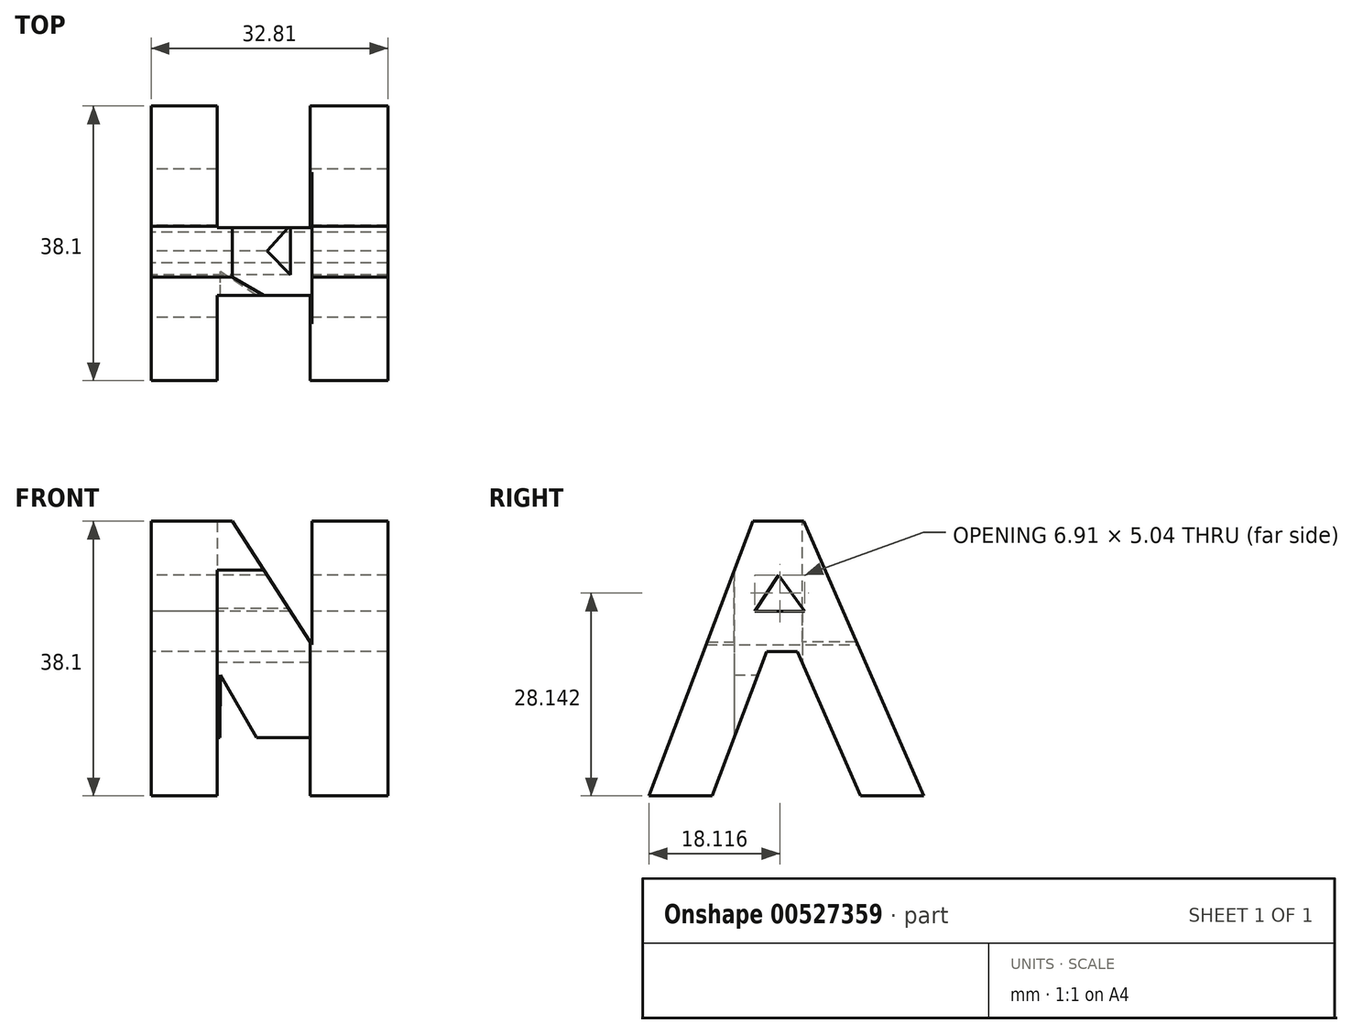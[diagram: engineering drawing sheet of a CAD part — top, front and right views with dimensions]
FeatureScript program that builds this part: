
annotation { "Feature Type Name" : "Feature", "Feature Type Description" : "" }
export const myFeature = defineFeature(function(context is Context, id is Id, definition is map)
    precondition{}
    {
        {
            var Q0;
            Q0=qCreatedBy(makeId("Front.planeOp"),FACE);
            var sketch = newSketch(context, id + "F0", { "sketchPlane" : qUnion([Q0])});
            skLineSegment(sketch, "E0", {"start": v(0, 0) * mm, "end": v(38.1, 0) * mm});
            skLineSegment(sketch, "E1", {"start": v(38.1, 0) * mm, "end": v(38.1, 38.1) * mm});
            skLineSegment(sketch, "E2", {"start": v(38.1, 38.1) * mm, "end": v(0, 38.1) * mm});
            skLineSegment(sketch, "E3", {"start": v(0, 38.1) * mm, "end": v(0, 0) * mm});
            skSolve(sketch);
        }
        {
            var Q0;
            Q0=qSketchRegion(id+"F0",true);
            extrude(context, id + "F1", {"entities" : qUnion([Q0]), "depth" : 38.1 * mm});
        }
        {
            var Q0;
            Q0=qCreatedBy(makeId("Right.planeOp"),FACE);
            var sketch = newSketch(context, id + "F2", { "sketchPlane" : qUnion([Q0])});
            skLineSegment(sketch, "E4", {"start": v(0, 0) * mm, "end": v(0, 38.1) * mm});
            skLineSegment(sketch, "E5", {"start": v(0, 38.1) * mm, "end": v(-38.1, 38.1) * mm});
            skLineSegment(sketch, "E6", {"start": v(-38.1, 38.1) * mm, "end": v(-38.1, 0) * mm});
            skLineSegment(sketch, "E7", {"start": v(-38.1, 0) * mm, "end": v(0, 0) * mm});
            skLineSegment(sketch, "E8", {"start": v(-38.1, 0) * mm, "end": v(-23.73, 38.1) * mm});
            skLineSegment(sketch, "E9", {"start": v(0, 0) * mm, "end": v(-16.67, 38.1) * mm});
            skLineSegment(sketch, "E10", {"start": v(-29.34, 0) * mm, "end": v(-21.78, 20.02) * mm});
            skLineSegment(sketch, "E11", {"start": v(-21.78, 20.02) * mm, "end": v(-17.52, 20.02) * mm});
            skLineSegment(sketch, "E12", {"start": v(-17.52, 20.02) * mm, "end": v(-8.76, 0) * mm});
            skLineSegment(sketch, "E13", {"start": v(-20.13, 25.62) * mm, "end": v(-16.53, 25.62) * mm});
            skLineSegment(sketch, "E14", {"start": v(-16.53, 25.62) * mm, "end": v(-20.13, 30.66) * mm});
            skLineSegment(sketch, "E15", {"start": v(-20.13, 30.66) * mm, "end": v(-23.44, 25.62) * mm});
            skLineSegment(sketch, "E16", {"start": v(-23.44, 25.62) * mm, "end": v(-20.13, 25.62) * mm});
            skSolve(sketch);
        }
        {
            var Q0;
            {var subQ0=sQuery(id+"F2.wireOp",EDGE,"E6");Q0=makeQuery(id+"F2.imprint","IMPRINT",FACE,{"disambiguationData":[TD([[makeQuery(id+"F2.imprint","IMPRINT",EDGE,{"derivedFrom":subQ0}),1.0]])]});}
            var Q1;
            {var subQ0=sQuery(id+"F2.wireOp",EDGE,"E10");Q1=makeQuery(id+"F2.imprint","IMPRINT",FACE,{"disambiguationData":[TD([[makeQuery(id+"F2.imprint","IMPRINT",EDGE,{"derivedFrom":subQ0}),-1.0]])]});}
            var Q2;
            {var subQ0=sQuery(id+"F2.wireOp",EDGE,"E4");Q2=makeQuery(id+"F2.imprint","IMPRINT",FACE,{"disambiguationData":[TD([[makeQuery(id+"F2.imprint","IMPRINT",EDGE,{"derivedFrom":subQ0}),1.0]])]});}
            var Q3;
            Q3=makeQuery(id+"F2.imprint","IMPRINT",FACE,{"disambiguationData":[TD([[makeQuery(id+"F2.imprint","IMPRINT",EDGE,{"derivedFrom":sQuery(id+"F2.wireOp",EDGE,"E13")}),1.0]])]});
            extrude(context, id + "F3", {"entities" : qUnion([Q0, Q1, Q2, Q3]), "operationType" : NewBodyOperationType.REMOVE, "depth" : 38.1 * mm});
        }
        {
            var Q0;
            Q0=qCreatedBy(makeId("Front.planeOp"),FACE);
            var sketch = newSketch(context, id + "F4", { "sketchPlane" : qUnion([Q0])});
            skLineSegment(sketch, "E17", {"start": v(0, 0) * mm, "end": v(38.1, 0) * mm});
            skLineSegment(sketch, "E18", {"start": v(38.1, 0) * mm, "end": v(38.1, 38.1) * mm});
            skLineSegment(sketch, "E19", {"start": v(38.1, 38.1) * mm, "end": v(0, 38.1) * mm});
            skLineSegment(sketch, "E20", {"start": v(0, 38.1) * mm, "end": v(0, 0) * mm});
            skLineSegment(sketch, "E21", {"start": v(13.19, 38.1) * mm, "end": v(24.25, 20.99) * mm});
            skLineSegment(sketch, "E22", {"start": v(11.37, 0) * mm, "end": v(11.56, 16.82) * mm});
            skLineSegment(sketch, "E23", {"start": v(11.56, 16.82) * mm, "end": v(21.16, 0) * mm});
            skLineSegment(sketch, "E24", {"start": v(24.25, 20.99) * mm, "end": v(24.25, 38.1) * mm});
            skLineSegment(sketch, "E25", {"start": v(34.76, 38.1) * mm, "end": v(34.76, 0) * mm});
            skLineSegment(sketch, "E26", {"start": v(1.95, 38.1) * mm, "end": v(1.95, 0) * mm});
            skSolve(sketch);
        }
        {
            var Q0;
            {var subQ0=sQuery(id+"F4.wireOp",EDGE,"E18");Q0=makeQuery(id+"F4.imprint","IMPRINT",FACE,{"disambiguationData":[TD([[makeQuery(id+"F4.imprint","IMPRINT",EDGE,{"derivedFrom":subQ0}),1.0]])]});}
            var Q1;
            {var subQ0=sQuery(id+"F4.wireOp",EDGE,"E21");Q1=makeQuery(id+"F4.imprint","IMPRINT",FACE,{"disambiguationData":[TD([[makeQuery(id+"F4.imprint","IMPRINT",EDGE,{"derivedFrom":subQ0}),1.0]])]});}
            var Q2;
            {var subQ0=sQuery(id+"F4.wireOp",EDGE,"E22");Q2=makeQuery(id+"F4.imprint","IMPRINT",FACE,{"disambiguationData":[TD([[makeQuery(id+"F4.imprint","IMPRINT",EDGE,{"derivedFrom":subQ0}),-1.0]])]});}
            var Q3;
            {var subQ0=sQuery(id+"F4.wireOp",EDGE,"E20");Q3=makeQuery(id+"F4.imprint","IMPRINT",FACE,{"disambiguationData":[TD([[makeQuery(id+"F4.imprint","IMPRINT",EDGE,{"derivedFrom":subQ0}),1.0]])]});}
            extrude(context, id + "F5", {"entities" : qUnion([Q0, Q1, Q2, Q3]), "operationType" : NewBodyOperationType.REMOVE, "depth" : 38.1 * mm});
        }
        {
            var Q0;
            Q0=qCreatedBy(makeId("Top.planeOp"),FACE);
            var sketch = newSketch(context, id + "F6", { "sketchPlane" : qUnion([Q0])});
            skLineSegment(sketch, "E27", {"start": v(0, 0) * mm, "end": v(38.1, 0) * mm});
            skLineSegment(sketch, "E28", {"start": v(38.1, 0) * mm, "end": v(38.1, -38.1) * mm});
            skLineSegment(sketch, "E29", {"start": v(38.1, -38.1) * mm, "end": v(0, -38.1) * mm});
            skLineSegment(sketch, "E30", {"start": v(0, -38.1) * mm, "end": v(0, 0) * mm});
            skLineSegment(sketch, "E31", {"start": v(11.12, 0) * mm, "end": v(11.12, -16.86) * mm});
            skLineSegment(sketch, "E32", {"start": v(11.12, -16.86) * mm, "end": v(24, -16.86) * mm});
            skLineSegment(sketch, "E33", {"start": v(24, -16.86) * mm, "end": v(24, 0) * mm});
            skLineSegment(sketch, "E34", {"start": v(11.12, -38.1) * mm, "end": v(11.12, -26.29) * mm});
            skLineSegment(sketch, "E35", {"start": v(11.12, -26.29) * mm, "end": v(24, -26.29) * mm});
            skLineSegment(sketch, "E36", {"start": v(24, -26.29) * mm, "end": v(24, -38.1) * mm});
            skLineSegment(sketch, "E37", {"start": v(34.93, 0) * mm, "end": v(34.93, -38.1) * mm});
            skLineSegment(sketch, "E38", {"start": v(1.93, 0) * mm, "end": v(1.93, -38.1) * mm});
            skSolve(sketch);
        }
        {
            var Q0;
            {var subQ0=sQuery(id+"F6.wireOp",EDGE,"E30");Q0=makeQuery(id+"F6.imprint","IMPRINT",FACE,{"disambiguationData":[TD([[makeQuery(id+"F6.imprint","IMPRINT",EDGE,{"derivedFrom":subQ0}),-1.0]])]});}
            var Q1;
            {var subQ0=sQuery(id+"F6.wireOp",EDGE,"E31");Q1=makeQuery(id+"F6.imprint","IMPRINT",FACE,{"disambiguationData":[TD([[makeQuery(id+"F6.imprint","IMPRINT",EDGE,{"derivedFrom":subQ0}),1.0]])]});}
            var Q2;
            {var subQ0=sQuery(id+"F6.wireOp",EDGE,"E34");Q2=makeQuery(id+"F6.imprint","IMPRINT",FACE,{"disambiguationData":[TD([[makeQuery(id+"F6.imprint","IMPRINT",EDGE,{"derivedFrom":subQ0}),-1.0]])]});}
            var Q3;
            {var subQ0=sQuery(id+"F6.wireOp",EDGE,"E28");Q3=makeQuery(id+"F6.imprint","IMPRINT",FACE,{"disambiguationData":[TD([[makeQuery(id+"F6.imprint","IMPRINT",EDGE,{"derivedFrom":subQ0}),-1.0]])]});}
            extrude(context, id + "F7", {"entities" : qUnion([Q0, Q1, Q2, Q3]), "operationType" : NewBodyOperationType.REMOVE, "depth" : 38.1 * mm});
        }
    });
